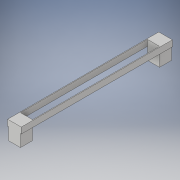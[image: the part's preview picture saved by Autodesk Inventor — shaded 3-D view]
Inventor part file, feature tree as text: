
AUTODESK INVENTOR PART (.ipt)
format: ipt  version: 2018 (Build 220112000, 112)  size: 124,416 bytes
history: native  units: in
note: dims shown in document units (in); Inventor stores cm internally (conversion verified against a paired STEP export)
features: extrude x3, sketch x3
ambient origin geometry x8: Origin, YZ Plane, XZ Plane, XY Plane, X Axis, Y Axis, Z Axis, Center Point
bodies: Solid1 (feature_tree)
feature tree (6):
  extrude  "Extrusion1"  Depth=3.0in TaperAngle=0.0deg
  extrude  "Extrusion2"  Depth=0.125in TaperAngle=0.0deg
  extrude  "Extrusion3"  Depth=21.0in
  sketch  "Sketch1"  dims[d0=2.0in d2=3.0in d3=0.0in]
  sketch  "Sketch2"  dims[d4=1.0in d5=0.125in d6=0.0in]
  sketch  "Sketch3"  dims[d8=0.125in d9=0.0in d10=21.0in d11=25.0in]
